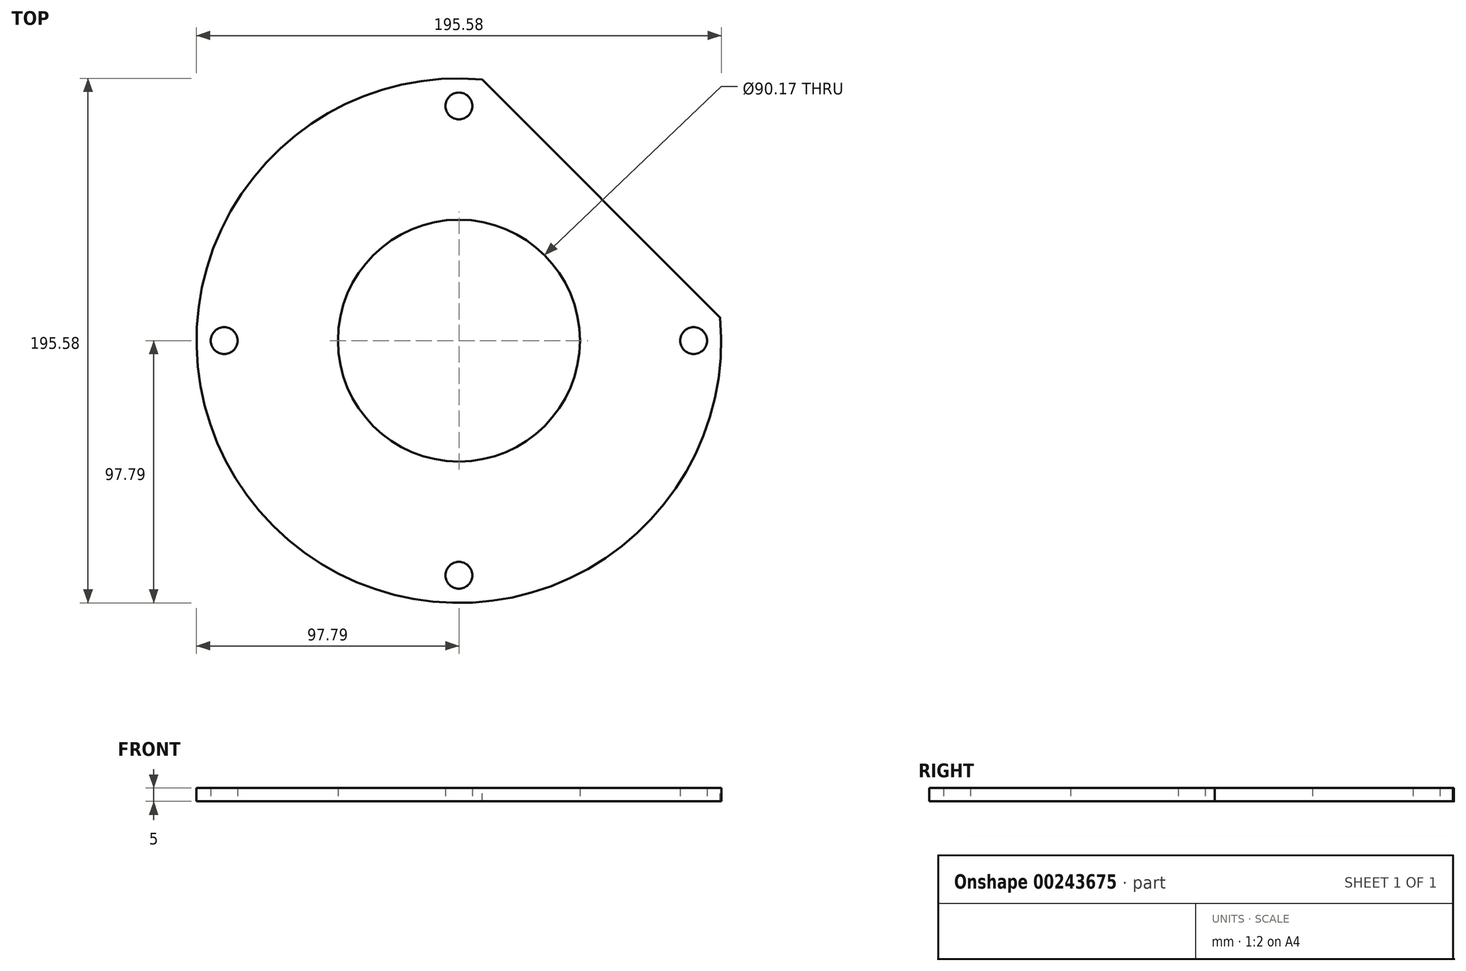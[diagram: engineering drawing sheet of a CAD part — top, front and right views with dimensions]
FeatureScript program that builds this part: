
annotation { "Feature Type Name" : "Feature", "Feature Type Description" : "" }
export const myFeature = defineFeature(function(context is Context, id is Id, definition is map)
    precondition{}
    {
        {
            var Q0;
            Q0=qCreatedBy(makeId("Top.planeOp"),FACE);
            var sketch = newSketch(context, id + "F0", { "sketchPlane" : qUnion([Q0])});
            skCircle(sketch, "E0", {"center": v(0, 0) * mm, "radius": 97.8 * mm});
            skLineSegment(sketch, "E1", {"start": v(0, 0) * mm, "end": v(0, 87.5) * mm, "construction": true});
            skCircle(sketch, "E2", {"center": v(0, 87.5) * mm, "radius": 5 * mm});
            skCircle(sketch, "E3.1.0", {"center": v(-87.5, 0) * mm, "radius": 5 * mm});
            skCircle(sketch, "E3.2.0", {"center": v(0, -87.5) * mm, "radius": 5 * mm});
            skCircle(sketch, "E3.3.0", {"center": v(87.5, 0) * mm, "radius": 5 * mm});
            skCircle(sketch, "E4", {"center": v(0, 0) * mm, "radius": 45.09 * mm});
            skSolve(sketch);
        }
        {
            var Q0;
            Q0=makeQuery(id+"F0.imprint","IMPRINT",FACE,{"disambiguationData":[TD([[makeQuery(id+"F0.imprint","IMPRINT",EDGE,{"derivedFrom":sQuery(id+"F0.wireOp",EDGE,"E0")}),1.0]])]});
            var Q1;
            {var subQ0=sQuery(id+"F0.wireOp",EDGE,"96d0f191-ea97-4706-a608-2a5a91b9ace0.15.0");var subQ1=sQuery(id+"F0.wireOp",EDGE,"aod9mALd-i6De-WTGj-Mxtv-1n9LFqxkPrRi");var subQ2=makeQuery(id+"F0.imprint","INTERSECT",VERTEX,{"derivedFrom":[subQ1,subQ0]});Q1=makeQuery(id+"F0.imprint","IMPRINT",FACE,{"disambiguationData":[TD([[makeQuery(id+"F0.imprint","IMPRINT",EDGE,{"disambiguationData":[TD([[subQ2,1.0]])],"derivedFrom":subQ1}),1.0]])]});}
            var Q2;
            {var subQ0=sQuery(id+"F0.wireOp",EDGE,"96d0f191-ea97-4706-a608-2a5a91b9ace0.16.0");var subQ1=sQuery(id+"F0.wireOp",EDGE,"aod9mALd-i6De-WTGj-Mxtv-1n9LFqxkPrRi");var subQ2=makeQuery(id+"F0.imprint","INTERSECT",VERTEX,{"derivedFrom":[subQ1,subQ0]});Q2=makeQuery(id+"F0.imprint","IMPRINT",FACE,{"disambiguationData":[TD([[makeQuery(id+"F0.imprint","IMPRINT",EDGE,{"disambiguationData":[TD([[subQ2,1.0]])],"derivedFrom":subQ1}),1.0]])]});}
            var Q3;
            {var subQ0=sQuery(id+"F0.wireOp",EDGE,"96d0f191-ea97-4706-a608-2a5a91b9ace0.17.0");var subQ1=sQuery(id+"F0.wireOp",EDGE,"aod9mALd-i6De-WTGj-Mxtv-1n9LFqxkPrRi");var subQ2=makeQuery(id+"F0.imprint","INTERSECT",VERTEX,{"derivedFrom":[subQ1,subQ0]});Q3=makeQuery(id+"F0.imprint","IMPRINT",FACE,{"disambiguationData":[TD([[makeQuery(id+"F0.imprint","IMPRINT",EDGE,{"disambiguationData":[TD([[subQ2,1.0]])],"derivedFrom":subQ1}),1.0]])]});}
            var Q4;
            {var subQ0=sQuery(id+"F0.wireOp",EDGE,"mrVKx09Z-qbiG-AknJ-Sl6Q-Vrd00Q10s6kT");var subQ1=sQuery(id+"F0.wireOp",EDGE,"aod9mALd-i6De-WTGj-Mxtv-1n9LFqxkPrRi");var subQ2=makeQuery(id+"F0.imprint","INTERSECT",VERTEX,{"derivedFrom":[subQ1,subQ0]});Q4=makeQuery(id+"F0.imprint","IMPRINT",FACE,{"disambiguationData":[TD([[makeQuery(id+"F0.imprint","IMPRINT",EDGE,{"disambiguationData":[TD([[subQ2,1.0]])],"derivedFrom":subQ1}),1.0]])]});}
            var Q5;
            {var subQ0=sQuery(id+"F0.wireOp",EDGE,"96d0f191-ea97-4706-a608-2a5a91b9ace0.1.0");var subQ1=sQuery(id+"F0.wireOp",EDGE,"aod9mALd-i6De-WTGj-Mxtv-1n9LFqxkPrRi");var subQ2=makeQuery(id+"F0.imprint","INTERSECT",VERTEX,{"derivedFrom":[subQ1,subQ0]});Q5=makeQuery(id+"F0.imprint","IMPRINT",FACE,{"disambiguationData":[TD([[makeQuery(id+"F0.imprint","IMPRINT",EDGE,{"disambiguationData":[TD([[subQ2,1.0]])],"derivedFrom":subQ1}),1.0]])]});}
            var Q6;
            {var subQ0=sQuery(id+"F0.wireOp",EDGE,"96d0f191-ea97-4706-a608-2a5a91b9ace0.2.0");var subQ1=sQuery(id+"F0.wireOp",EDGE,"aod9mALd-i6De-WTGj-Mxtv-1n9LFqxkPrRi");var subQ2=makeQuery(id+"F0.imprint","INTERSECT",VERTEX,{"derivedFrom":[subQ1,subQ0]});Q6=makeQuery(id+"F0.imprint","IMPRINT",FACE,{"disambiguationData":[TD([[makeQuery(id+"F0.imprint","IMPRINT",EDGE,{"disambiguationData":[TD([[subQ2,1.0]])],"derivedFrom":subQ1}),1.0]])]});}
            var Q7;
            {var subQ0=sQuery(id+"F0.wireOp",EDGE,"96d0f191-ea97-4706-a608-2a5a91b9ace0.3.0");var subQ1=sQuery(id+"F0.wireOp",EDGE,"aod9mALd-i6De-WTGj-Mxtv-1n9LFqxkPrRi");var subQ2=makeQuery(id+"F0.imprint","INTERSECT",VERTEX,{"derivedFrom":[subQ1,subQ0]});Q7=makeQuery(id+"F0.imprint","IMPRINT",FACE,{"disambiguationData":[TD([[makeQuery(id+"F0.imprint","IMPRINT",EDGE,{"disambiguationData":[TD([[subQ2,1.0]])],"derivedFrom":subQ1}),1.0]])]});}
            var Q8;
            {var subQ0=sQuery(id+"F0.wireOp",EDGE,"96d0f191-ea97-4706-a608-2a5a91b9ace0.4.0");var subQ1=sQuery(id+"F0.wireOp",EDGE,"aod9mALd-i6De-WTGj-Mxtv-1n9LFqxkPrRi");var subQ2=makeQuery(id+"F0.imprint","INTERSECT",VERTEX,{"derivedFrom":[subQ1,subQ0]});Q8=makeQuery(id+"F0.imprint","IMPRINT",FACE,{"disambiguationData":[TD([[makeQuery(id+"F0.imprint","IMPRINT",EDGE,{"disambiguationData":[TD([[subQ2,1.0]])],"derivedFrom":subQ1}),1.0]])]});}
            var Q9;
            {var subQ0=sQuery(id+"F0.wireOp",EDGE,"96d0f191-ea97-4706-a608-2a5a91b9ace0.5.0");var subQ1=sQuery(id+"F0.wireOp",EDGE,"aod9mALd-i6De-WTGj-Mxtv-1n9LFqxkPrRi");var subQ2=makeQuery(id+"F0.imprint","INTERSECT",VERTEX,{"derivedFrom":[subQ1,subQ0]});Q9=makeQuery(id+"F0.imprint","IMPRINT",FACE,{"disambiguationData":[TD([[makeQuery(id+"F0.imprint","IMPRINT",EDGE,{"disambiguationData":[TD([[subQ2,1.0]])],"derivedFrom":subQ1}),1.0]])]});}
            var Q10;
            {var subQ0=sQuery(id+"F0.wireOp",EDGE,"96d0f191-ea97-4706-a608-2a5a91b9ace0.6.0");var subQ1=sQuery(id+"F0.wireOp",EDGE,"aod9mALd-i6De-WTGj-Mxtv-1n9LFqxkPrRi");var subQ2=makeQuery(id+"F0.imprint","INTERSECT",VERTEX,{"derivedFrom":[subQ1,subQ0]});Q10=makeQuery(id+"F0.imprint","IMPRINT",FACE,{"disambiguationData":[TD([[makeQuery(id+"F0.imprint","IMPRINT",EDGE,{"disambiguationData":[TD([[subQ2,1.0]])],"derivedFrom":subQ1}),1.0]])]});}
            var Q11;
            {var subQ0=sQuery(id+"F0.wireOp",EDGE,"96d0f191-ea97-4706-a608-2a5a91b9ace0.7.0");var subQ1=sQuery(id+"F0.wireOp",EDGE,"aod9mALd-i6De-WTGj-Mxtv-1n9LFqxkPrRi");var subQ2=makeQuery(id+"F0.imprint","INTERSECT",VERTEX,{"derivedFrom":[subQ1,subQ0]});Q11=makeQuery(id+"F0.imprint","IMPRINT",FACE,{"disambiguationData":[TD([[makeQuery(id+"F0.imprint","IMPRINT",EDGE,{"disambiguationData":[TD([[subQ2,1.0]])],"derivedFrom":subQ1}),1.0]])]});}
            var Q12;
            {var subQ0=sQuery(id+"F0.wireOp",EDGE,"96d0f191-ea97-4706-a608-2a5a91b9ace0.8.0");var subQ1=sQuery(id+"F0.wireOp",EDGE,"aod9mALd-i6De-WTGj-Mxtv-1n9LFqxkPrRi");var subQ2=makeQuery(id+"F0.imprint","INTERSECT",VERTEX,{"derivedFrom":[subQ1,subQ0]});Q12=makeQuery(id+"F0.imprint","IMPRINT",FACE,{"disambiguationData":[TD([[makeQuery(id+"F0.imprint","IMPRINT",EDGE,{"disambiguationData":[TD([[subQ2,1.0]])],"derivedFrom":subQ1}),1.0]])]});}
            var Q13;
            {var subQ0=sQuery(id+"F0.wireOp",EDGE,"96d0f191-ea97-4706-a608-2a5a91b9ace0.9.0");var subQ1=sQuery(id+"F0.wireOp",EDGE,"aod9mALd-i6De-WTGj-Mxtv-1n9LFqxkPrRi");var subQ2=makeQuery(id+"F0.imprint","INTERSECT",VERTEX,{"derivedFrom":[subQ1,subQ0]});Q13=makeQuery(id+"F0.imprint","IMPRINT",FACE,{"disambiguationData":[TD([[makeQuery(id+"F0.imprint","IMPRINT",EDGE,{"disambiguationData":[TD([[subQ2,1.0]])],"derivedFrom":subQ1}),1.0]])]});}
            var Q14;
            {var subQ0=sQuery(id+"F0.wireOp",EDGE,"96d0f191-ea97-4706-a608-2a5a91b9ace0.10.0");var subQ1=sQuery(id+"F0.wireOp",EDGE,"aod9mALd-i6De-WTGj-Mxtv-1n9LFqxkPrRi");var subQ2=makeQuery(id+"F0.imprint","INTERSECT",VERTEX,{"derivedFrom":[subQ1,subQ0]});Q14=makeQuery(id+"F0.imprint","IMPRINT",FACE,{"disambiguationData":[TD([[makeQuery(id+"F0.imprint","IMPRINT",EDGE,{"disambiguationData":[TD([[subQ2,1.0]])],"derivedFrom":subQ1}),1.0]])]});}
            var Q15;
            {var subQ0=sQuery(id+"F0.wireOp",EDGE,"96d0f191-ea97-4706-a608-2a5a91b9ace0.11.0");var subQ1=sQuery(id+"F0.wireOp",EDGE,"aod9mALd-i6De-WTGj-Mxtv-1n9LFqxkPrRi");var subQ2=makeQuery(id+"F0.imprint","INTERSECT",VERTEX,{"derivedFrom":[subQ1,subQ0]});Q15=makeQuery(id+"F0.imprint","IMPRINT",FACE,{"disambiguationData":[TD([[makeQuery(id+"F0.imprint","IMPRINT",EDGE,{"disambiguationData":[TD([[subQ2,1.0]])],"derivedFrom":subQ1}),1.0]])]});}
            var Q16;
            {var subQ0=sQuery(id+"F0.wireOp",EDGE,"96d0f191-ea97-4706-a608-2a5a91b9ace0.12.0");var subQ1=sQuery(id+"F0.wireOp",EDGE,"aod9mALd-i6De-WTGj-Mxtv-1n9LFqxkPrRi");var subQ2=makeQuery(id+"F0.imprint","INTERSECT",VERTEX,{"derivedFrom":[subQ1,subQ0]});Q16=makeQuery(id+"F0.imprint","IMPRINT",FACE,{"disambiguationData":[TD([[makeQuery(id+"F0.imprint","IMPRINT",EDGE,{"disambiguationData":[TD([[subQ2,1.0]])],"derivedFrom":subQ1}),1.0]])]});}
            var Q17;
            {var subQ0=sQuery(id+"F0.wireOp",EDGE,"96d0f191-ea97-4706-a608-2a5a91b9ace0.13.0");var subQ1=sQuery(id+"F0.wireOp",EDGE,"aod9mALd-i6De-WTGj-Mxtv-1n9LFqxkPrRi");var subQ2=makeQuery(id+"F0.imprint","INTERSECT",VERTEX,{"derivedFrom":[subQ1,subQ0]});Q17=makeQuery(id+"F0.imprint","IMPRINT",FACE,{"disambiguationData":[TD([[makeQuery(id+"F0.imprint","IMPRINT",EDGE,{"disambiguationData":[TD([[subQ2,1.0]])],"derivedFrom":subQ1}),1.0]])]});}
            var Q18;
            {var subQ0=sQuery(id+"F0.wireOp",EDGE,"96d0f191-ea97-4706-a608-2a5a91b9ace0.14.0");var subQ1=sQuery(id+"F0.wireOp",EDGE,"aod9mALd-i6De-WTGj-Mxtv-1n9LFqxkPrRi");var subQ2=makeQuery(id+"F0.imprint","INTERSECT",VERTEX,{"derivedFrom":[subQ1,subQ0]});Q18=makeQuery(id+"F0.imprint","IMPRINT",FACE,{"disambiguationData":[TD([[makeQuery(id+"F0.imprint","IMPRINT",EDGE,{"disambiguationData":[TD([[subQ2,1.0]])],"derivedFrom":subQ1}),1.0]])]});}
            extrude(context, id + "F1", {"entities" : qUnion([Q0, Q1, Q2, Q3, Q4, Q5, Q6, Q7, Q8, Q9, Q10, Q11, Q12, Q13, Q14, Q15, Q16, Q17, Q18]), "depth" : 5 * mm});
        }
        {
            var Q0;
            Q0=makeQuery(id+"F1.opExtrude","CAP_FACE",FACE,{"disambiguationData":[OSD([sQuery(id+"F0.wireOp",EDGE,"E0"),sQuery(id+"F0.wireOp",EDGE,"E2"),sQuery(id+"F0.wireOp",EDGE,"E3.1.0"),sQuery(id+"F0.wireOp",EDGE,"E3.2.0"),sQuery(id+"F0.wireOp",EDGE,"E3.3.0"),sQuery(id+"F0.wireOp",EDGE,"E4")])],"isStart":false});
            var sketch = newSketch(context, id + "F2", { "sketchPlane" : qUnion([Q0])});
            skLineSegment(sketch, "E5", {"start": v(0, 87.5) * mm, "end": v(0, 0) * mm, "construction": true});
            skLineSegment(sketch, "E6", {"start": v(0, 0) * mm, "end": v(53.03, 53.03) * mm, "construction": true});
            skLineSegment(sketch, "E7", {"start": v(8.66, 97.4) * mm, "end": v(97.4, 8.66) * mm});
            skArc(sketch, "E8", {"start": v(97.4, 8.66) * mm, "mid": v(69.15, 69.15) * mm, "end": v(8.66, 97.4) * mm});
            skSolve(sketch);
        }
        {
            var Q0;
            Q0 = qSketchRegion(id + "F2", true);
            extrude(context, id + "F3", {"entities" : qUnion([Q0]), "operationType" : NewBodyOperationType.REMOVE, "endBound" : BoundingType.THROUGH_ALL, "oppositeDirection" : true, "depth" : 25.4 * mm});
        }
    });
